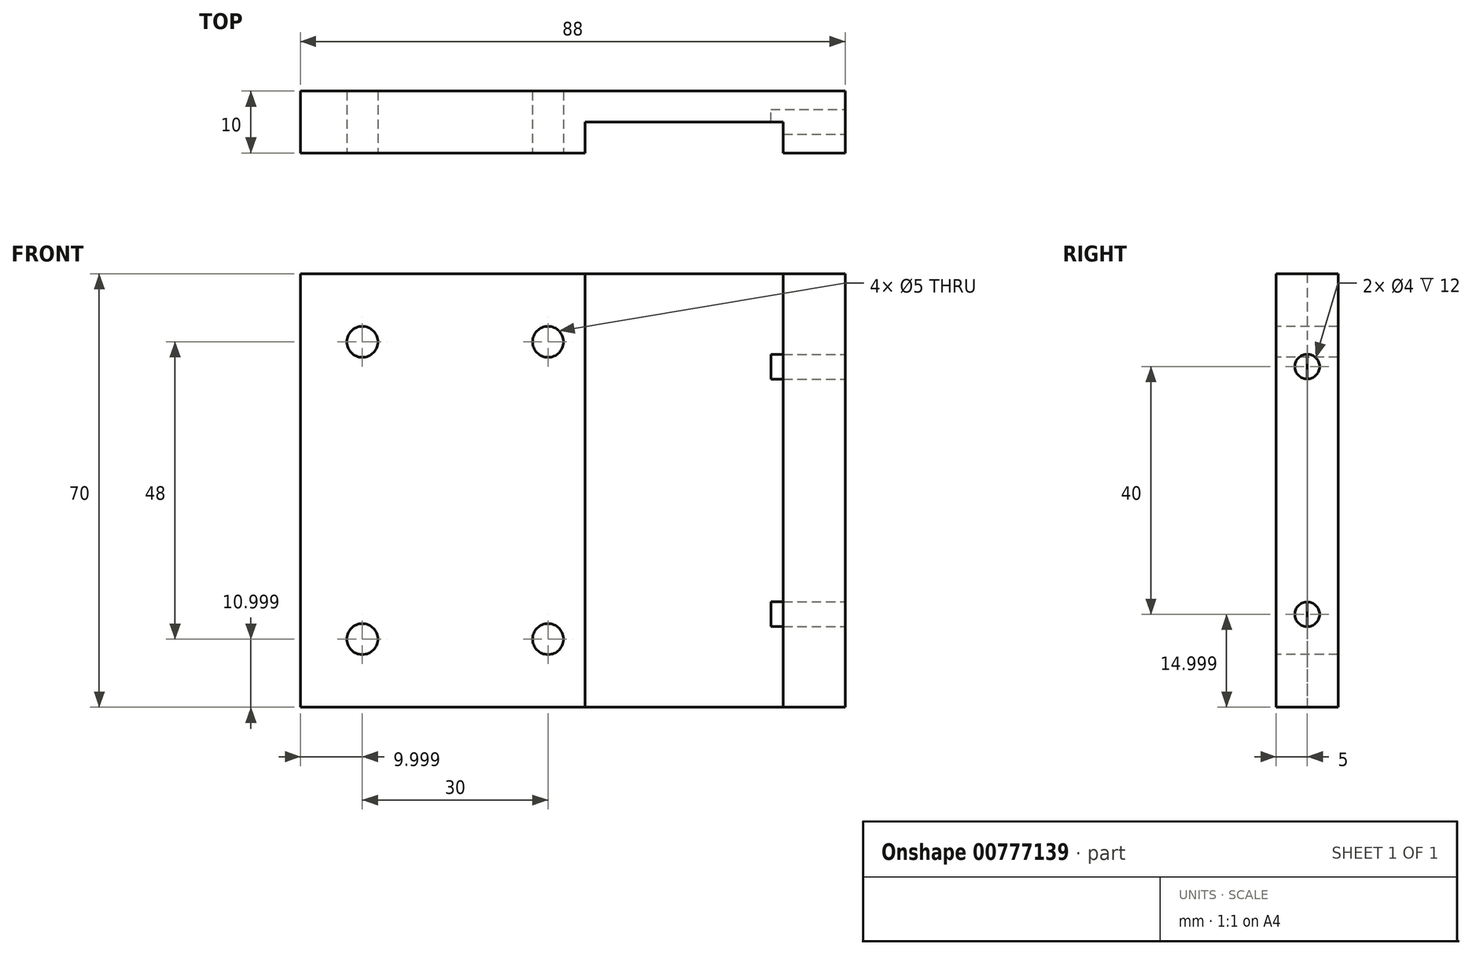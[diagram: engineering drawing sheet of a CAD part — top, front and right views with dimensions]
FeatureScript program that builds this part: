
annotation { "Feature Type Name" : "Feature", "Feature Type Description" : "" }
export const myFeature = defineFeature(function(context is Context, id is Id, definition is map)
    precondition{}
    {
        {
            var Q0;
            Q0=qCreatedBy(makeId("Front.planeOp"),FACE);
            var sketch = newSketch(context, id + "F0", { "sketchPlane" : qUnion([Q0])});
            skLineSegment(sketch, "E0.bottom", {"start": v(-112.96, 81.39) * mm, "end": v(-24.96, 81.39) * mm});
            skLineSegment(sketch, "E0.top", {"start": v(-112.96, 11.39) * mm, "end": v(-24.96, 11.39) * mm});
            skLineSegment(sketch, "E0.left", {"start": v(-112.96, 81.39) * mm, "end": v(-112.96, 11.39) * mm});
            skLineSegment(sketch, "E0.right", {"start": v(-24.96, 81.39) * mm, "end": v(-24.96, 11.39) * mm});
            skSolve(sketch);
        }
        {
            var Q0;
            Q0 = qSketchRegion(id + "F0", true);
            extrude(context, id + "F1", {"entities" : qUnion([Q0]), "depth" : 10 * mm, "offsetDistance" : 25 * mm});
        }
        {
            var Q0;
            Q0=makeQuery(id+"F1.opExtrude","CAP_FACE",FACE,{"disambiguationData":[OSD([sQuery(id+"F0.wireOp",EDGE,"E0.bottom"),sQuery(id+"F0.wireOp",EDGE,"E0.top"),sQuery(id+"F0.wireOp",EDGE,"E0.left"),sQuery(id+"F0.wireOp",EDGE,"E0.right")])],"isStart":false});
            var sketch = newSketch(context, id + "F2", { "sketchPlane" : qUnion([Q0])});
            skLineSegment(sketch, "E1.bottom", {"start": v(-66.96, 81.39) * mm, "end": v(-34.96, 81.39) * mm});
            skLineSegment(sketch, "E1.top", {"start": v(-66.96, 11.39) * mm, "end": v(-34.96, 11.39) * mm});
            skLineSegment(sketch, "E1.left", {"start": v(-66.96, 81.39) * mm, "end": v(-66.96, 11.39) * mm});
            skLineSegment(sketch, "E1.right", {"start": v(-34.96, 81.39) * mm, "end": v(-34.96, 11.39) * mm});
            skCircle(sketch, "E2", {"center": v(-102.96, 70.39) * mm, "radius": 2.5 * mm});
            skCircle(sketch, "E3", {"center": v(-72.96, 70.39) * mm, "radius": 2.5 * mm});
            skCircle(sketch, "E4", {"center": v(-102.96, 22.39) * mm, "radius": 2.5 * mm});
            skCircle(sketch, "E5", {"center": v(-72.96, 22.39) * mm, "radius": 2.5 * mm});
            skSolve(sketch);
        }
        {
            var Q0;
            Q0=makeQuery(id+"F2.imprint","IMPRINT",FACE,{"disambiguationData":[TD([[makeQuery(id+"F2.imprint","IMPRINT",EDGE,{"derivedFrom":sQuery(id+"F2.wireOp",EDGE,"E1.bottom")}),-1.0]])]});
            extrude(context, id + "F3", {"entities" : qUnion([Q0]), "operationType" : NewBodyOperationType.REMOVE, "oppositeDirection" : true, "depth" : 5 * mm, "offsetDistance" : 25 * mm});
        }
        {
            var Q0;
            Q0=makeQuery(id+"F2.imprint","IMPRINT",FACE,{"disambiguationData":[TD([[makeQuery(id+"F2.imprint","IMPRINT",EDGE,{"derivedFrom":sQuery(id+"F2.wireOp",EDGE,"E2")}),1.0]])]});
            var Q1;
            Q1=makeQuery(id+"F2.imprint","IMPRINT",FACE,{"disambiguationData":[TD([[makeQuery(id+"F2.imprint","IMPRINT",EDGE,{"derivedFrom":sQuery(id+"F2.wireOp",EDGE,"E3")}),1.0]])]});
            var Q2;
            Q2=makeQuery(id+"F2.imprint","IMPRINT",FACE,{"disambiguationData":[TD([[makeQuery(id+"F2.imprint","IMPRINT",EDGE,{"derivedFrom":sQuery(id+"F2.wireOp",EDGE,"E4")}),1.0]])]});
            var Q3;
            Q3=makeQuery(id+"F2.imprint","IMPRINT",FACE,{"disambiguationData":[TD([[makeQuery(id+"F2.imprint","IMPRINT",EDGE,{"derivedFrom":sQuery(id+"F2.wireOp",EDGE,"E5")}),1.0]])]});
            extrude(context, id + "F4", {"entities" : qUnion([Q0, Q1, Q2, Q3]), "operationType" : NewBodyOperationType.REMOVE, "endBound" : BoundingType.THROUGH_ALL, "oppositeDirection" : true, "depth" : 25 * mm, "offsetDistance" : 25 * mm});
        }
        {
            var Q0;
            Q0=makeQuery(id+"F1.opExtrude","SWEPT_FACE",FACE,{"disambiguationData":[OSD([sQuery(id+"F0.wireOp",EDGE,"E0.right")])]});
            var sketch = newSketch(context, id + "F5", { "sketchPlane" : qUnion([Q0])});
            skCircle(sketch, "E6", {"center": v(-5, 26.39) * mm, "radius": 2 * mm});
            skPoint(sketch, "E6.centerSnap0", {"position": v(-5, 11.39) * mm});
            skCircle(sketch, "E7", {"center": v(-5, 66.39) * mm, "radius": 2 * mm});
            skSolve(sketch);
        }
        {
            var Q0;
            Q0=makeQuery(id+"F5.imprint","IMPRINT",FACE,{"disambiguationData":[TD([[makeQuery(id+"F5.imprint","IMPRINT",EDGE,{"derivedFrom":sQuery(id+"F5.wireOp",EDGE,"E6")}),1.0]])]});
            var Q1;
            Q1=makeQuery(id+"F5.imprint","IMPRINT",FACE,{"disambiguationData":[TD([[makeQuery(id+"F5.imprint","IMPRINT",EDGE,{"derivedFrom":sQuery(id+"F5.wireOp",EDGE,"E7")}),1.0]])]});
            extrude(context, id + "F6", {"entities" : qUnion([Q0, Q1]), "operationType" : NewBodyOperationType.REMOVE, "oppositeDirection" : true, "depth" : 12 * mm, "offsetDistance" : 25 * mm});
        }
    });
